# Revit family: NICE20
name_source: partatom
category: Lighting Fixtures
units: mm (PartAtom-declared; Revit-internal decimal feet)

## family parameters
Cut with Voids When Loaded = No
Host = Face
Light Source = Yes
Maintain Annotation Orientation = Yes
Part Type = Normal
Room Calculation Point = No
Round Connector Dimension = Use Diameter
Shared = No

## types (6) — shared parameters
Color Filter = 16777215
Default Elevation = 1219 mm
Dimming Lamp Color Temperature Shift = <None>
Emit from Line Length = 610 mm
Manufacturer = LUXLIGHT
Tilt Angle = -90.00°
zero-valued in all types: LuxLight_Alto, LuxLight_AltoAreaLuminosa, LuxLight_Ancho, LuxLight_AnchoAreaLuminosa, LuxLight_Diametro, LuxLight_DiametroAreaLuminosa, LuxLight_Largo, LuxLight_LargoAreaLuminosa, LuxLight_ProtuberanciaTecho

## per-type parameters (varying)
| type | LuxLight_Amperios | LuxLight_Lumenes | LuxLight_Temperatura | LuxLight_Watios | Photometric Web File |
| LXRNI20192x | 350 | 1982 lm | 2700 K | 15 W | LXRNI202921 .ies |
| LXRNI20193x | 350 | 2011 lm | 3000 K | 15 W | LXRNI202931 .ies |
| LXRNI20194x | 350 | 2082 lm | 4000 K | 15 W | LXRNI202941 .ies |
| LXRNI20292x | 500 | 2643 lm | 2700 K | 20 W | LXRNI202921 .ies |
| LXRNI20293x | 500 | 2681 lm | 3000 K | 20 W | LXRNI202931 .ies |
| LXRNI20294x | 500 | 2776 lm | 4000 K | 20 W | LXRNI202941 .ies |

## geometry (parser evidence)
native form markers: Sweep x3
no freeform markers — native parametric forms only
